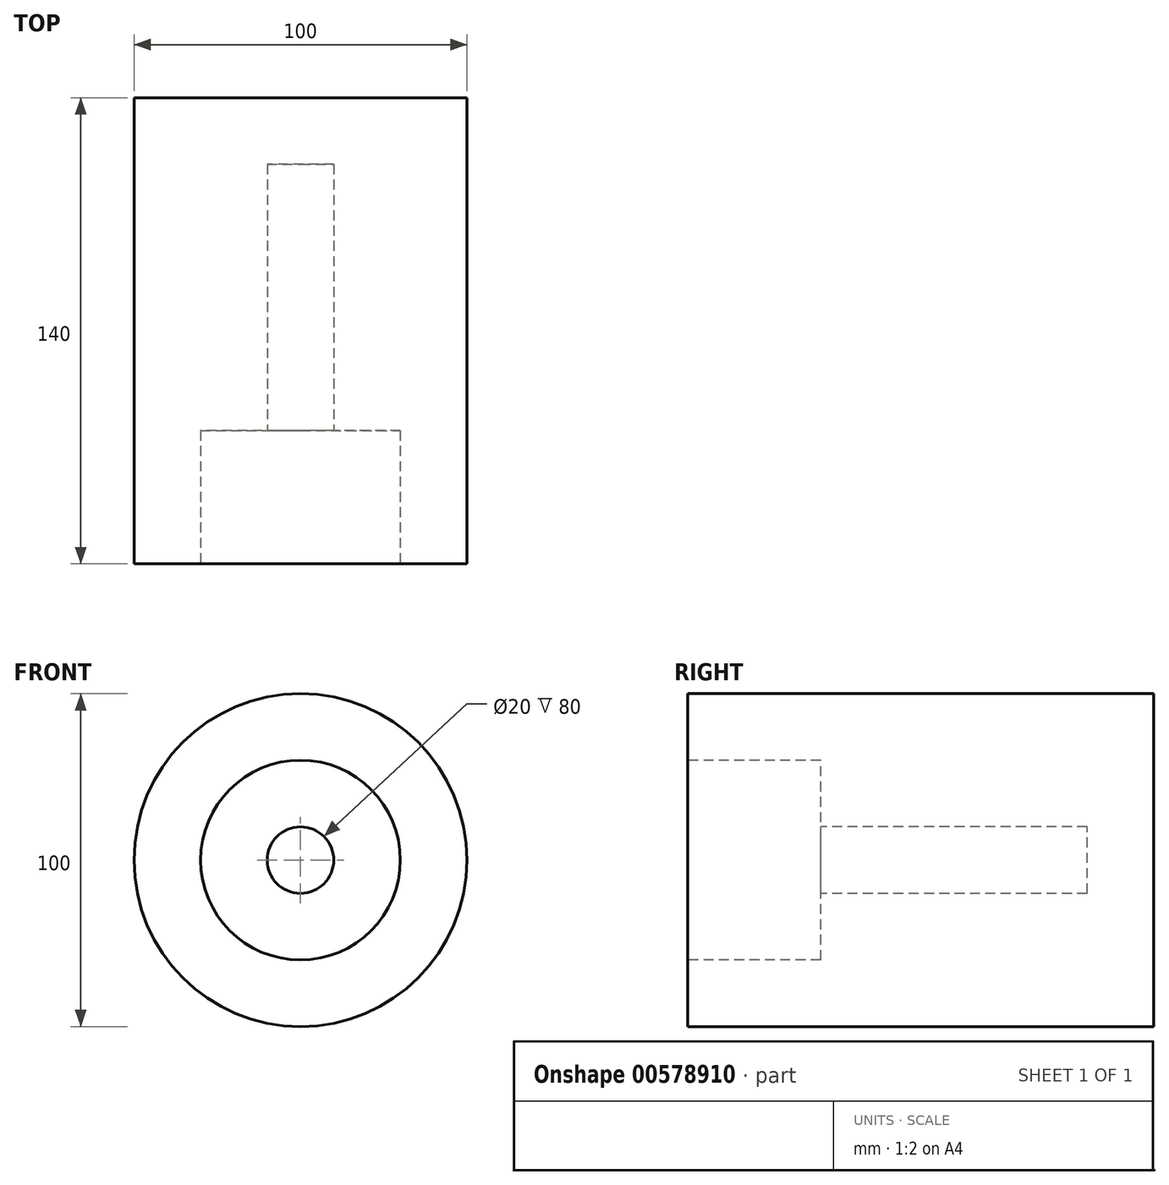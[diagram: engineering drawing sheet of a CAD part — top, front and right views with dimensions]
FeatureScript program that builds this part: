
annotation { "Feature Type Name" : "Feature", "Feature Type Description" : "" }
export const myFeature = defineFeature(function(context is Context, id is Id, definition is map)
    precondition{}
    {
        {
            var Q0;
            Q0=qCreatedBy(makeId("Front.planeOp"),FACE);
            var sketch = newSketch(context, id + "F0", { "sketchPlane" : qUnion([Q0])});
            skCircle(sketch, "E0", {"center": v(0, 0) * mm, "radius": 50 * mm});
            skSolve(sketch);
        }
        {
            var Q0;
            Q0 = qSketchRegion(id + "F0", true);
            extrude(context, id + "F1", {"entities" : qUnion([Q0]), "endBound" : BoundingType.SYMMETRIC, "depth" : 140 * mm, "offsetDistance" : 25 * mm});
        }
        {
            var Q0;
            Q0=makeQuery(id+"F1.opExtrude","CAP_FACE",FACE,{"disambiguationData":[OSD([sQuery(id+"F0.wireOp",EDGE,"E0")])],"isStart":false});
            var sketch = newSketch(context, id + "F2", { "sketchPlane" : qUnion([Q0])});
            skCircle(sketch, "E1", {"center": v(0, 0) * mm, "radius": 30 * mm});
            skSolve(sketch);
        }
        {
            var Q0;
            Q0=makeQuery(id+"F2.imprint","IMPRINT",FACE,{"disambiguationData":[TD([[makeQuery(id+"F2.imprint","IMPRINT",EDGE,{"derivedFrom":sQuery(id+"F2.wireOp",EDGE,"E1")}),1.0]])]});
            extrude(context, id + "F3", {"entities" : qUnion([Q0]), "operationType" : NewBodyOperationType.REMOVE, "oppositeDirection" : true, "depth" : 40 * mm, "offsetDistance" : 25 * mm});
        }
        {
            var Q0;
            Q0=makeQuery(id+"F3.boolean.opBoolean","COPY",FACE,{"derivedFrom":makeQuery(id+"F3.opExtrude","CAP_FACE",FACE,{"disambiguationData":[OSD([sQuery(id+"F2.wireOp",EDGE,"E1")])],"isStart":false})});
            var sketch = newSketch(context, id + "F4", { "sketchPlane" : qUnion([Q0])});
            skCircle(sketch, "E2", {"center": v(0, 0) * mm, "radius": 10 * mm});
            skSolve(sketch);
        }
        {
            var Q0;
            Q0 = qSketchRegion(id + "F4", true);
            extrude(context, id + "F5", {"entities" : qUnion([Q0]), "operationType" : NewBodyOperationType.REMOVE, "oppositeDirection" : true, "depth" : (120 - 40) * mm, "offsetDistance" : 25 * mm});
        }
    });
